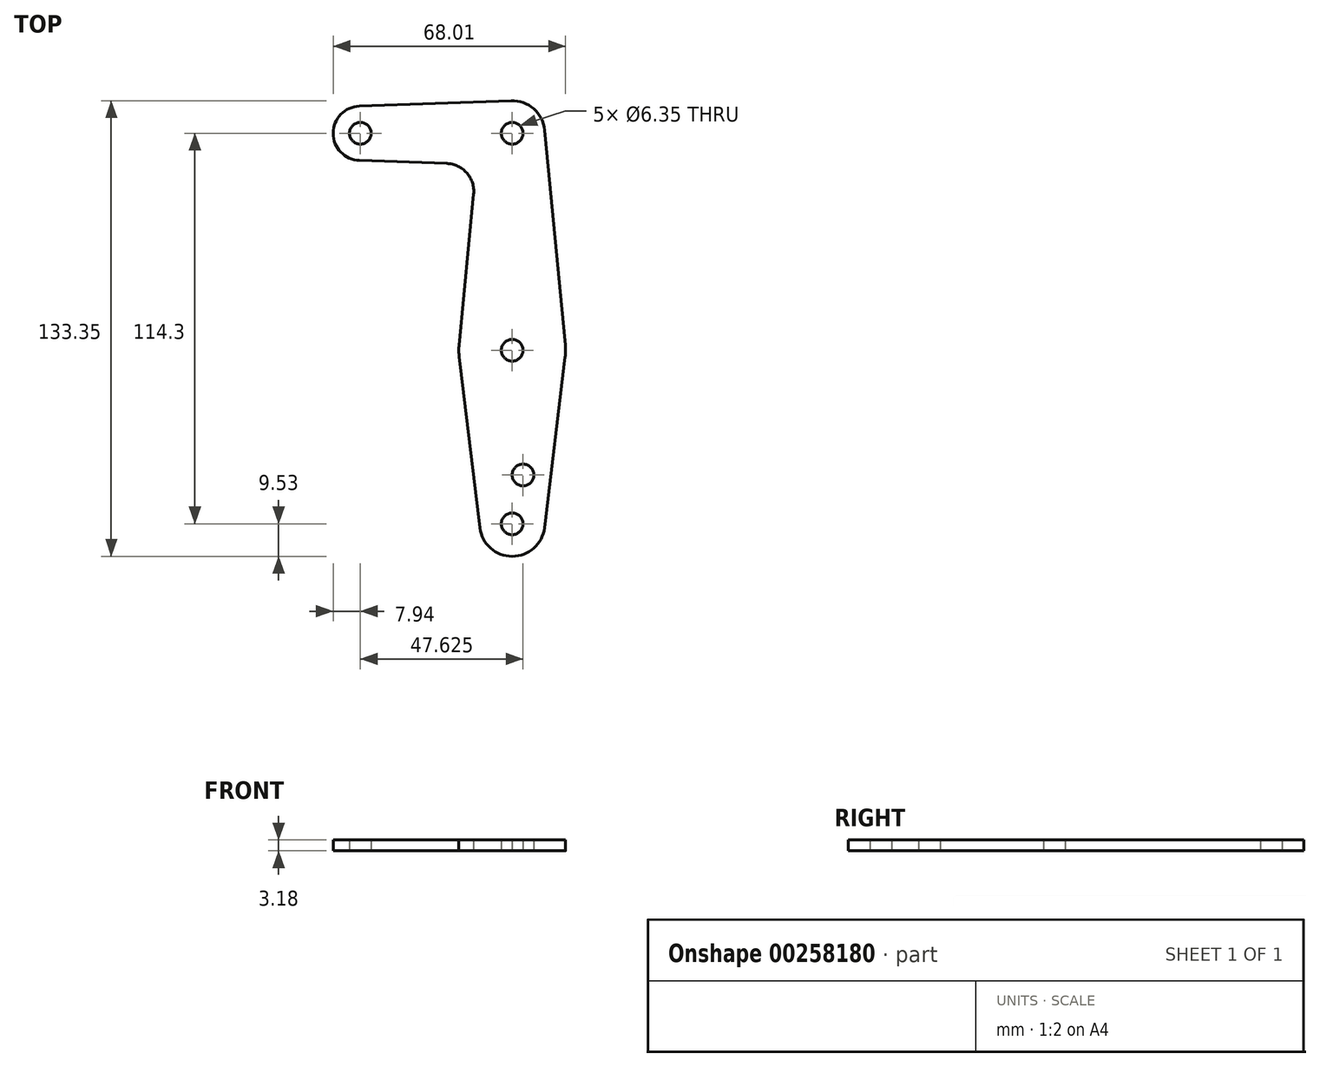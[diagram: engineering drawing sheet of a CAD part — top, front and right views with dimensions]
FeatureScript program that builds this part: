
annotation { "Feature Type Name" : "Feature", "Feature Type Description" : "" }
export const myFeature = defineFeature(function(context is Context, id is Id, definition is map)
    precondition{}
    {
        {
            var Q0;
            Q0=qCreatedBy(makeId("Top.planeOp"),FACE);
            var sketch = newSketch(context, id + "F0", { "sketchPlane" : qUnion([Q0])});
            skCircle(sketch, "E0", {"center": v(0, 0) * mm, "radius": 3.17 * mm});
            skLineSegment(sketch, "E1", {"start": v(0, 0) * mm, "end": v(-44.45, 0) * mm, "construction": true});
            skCircle(sketch, "E2", {"center": v(-44.45, 0) * mm, "radius": 3.18 * mm});
            skLineSegment(sketch, "E3", {"start": v(0, 0) * mm, "end": v(0, -63.5) * mm, "construction": true});
            skCircle(sketch, "E4", {"center": v(0, -63.5) * mm, "radius": 3.18 * mm});
            skLineSegment(sketch, "E5", {"start": v(0, -63.5) * mm, "end": v(0, -100.01) * mm, "construction": true});
            skLineSegment(sketch, "E6", {"start": v(0, -63.5) * mm, "end": v(0, -114.3) * mm});
            skCircle(sketch, "E7", {"center": v(0, -114.3) * mm, "radius": 3.18 * mm});
            skCircle(sketch, "E8", {"center": v(3.18, -100.01) * mm, "radius": 3.18 * mm});
            skCircle(sketch, "E9", {"center": v(-44.45, 0) * mm, "radius": 7.94 * mm});
            skCircle(sketch, "E10", {"center": v(0, 0) * mm, "radius": 9.53 * mm});
            skLineSegment(sketch, "E11", {"start": v(-44.73, 7.93) * mm, "end": v(0, 9.53) * mm});
            skLineSegment(sketch, "E12", {"start": v(-44.73, -7.93) * mm, "end": v(0, -9.53) * mm});
            skCircle(sketch, "E13", {"center": v(0, -63.5) * mm, "radius": 15.62 * mm});
            skCircle(sketch, "E14", {"center": v(0, -114.3) * mm, "radius": 9.53 * mm});
            skLineSegment(sketch, "E15", {"start": v(-15.5, -65.37) * mm, "end": v(-9.46, -115.44) * mm});
            skLineSegment(sketch, "E16", {"start": v(15.5, -65.37) * mm, "end": v(9.46, -115.44) * mm});
            skLineSegment(sketch, "E17", {"start": v(9.48, 0.91) * mm, "end": v(15.55, -62) * mm});
            skLineSegment(sketch, "E18", {"start": v(-9.48, 0.91) * mm, "end": v(-15.55, -62) * mm});
            skPoint(sketch, "E19.orphan", {"position": v(-15.5, -61.58) * mm});
            skSolve(sketch);
        }
        {
            var Q0;
            Q0 = qSketchRegion(id + "F0", true);
            extrude(context, id + "F1", {"entities" : qUnion([Q0]), "depth" : 3.17 * mm});
        }
        {
            var Q0;
            Q0=makeQuery(id+"F1.opExtrude","SWEPT_EDGE",EDGE,{"disambiguationData":[OSD([sQuery(id+"F0.wireOp",EDGE,"E12"),sQuery(id+"F0.wireOp",EDGE,"E18")])]});
            fillet(context, id + "F2", {"entities" : qUnion([Q0]), "radius" : 8.2 * mm, "tangentPropagation" : true, "allowEdgeOverflow" : false});
        }
    });
